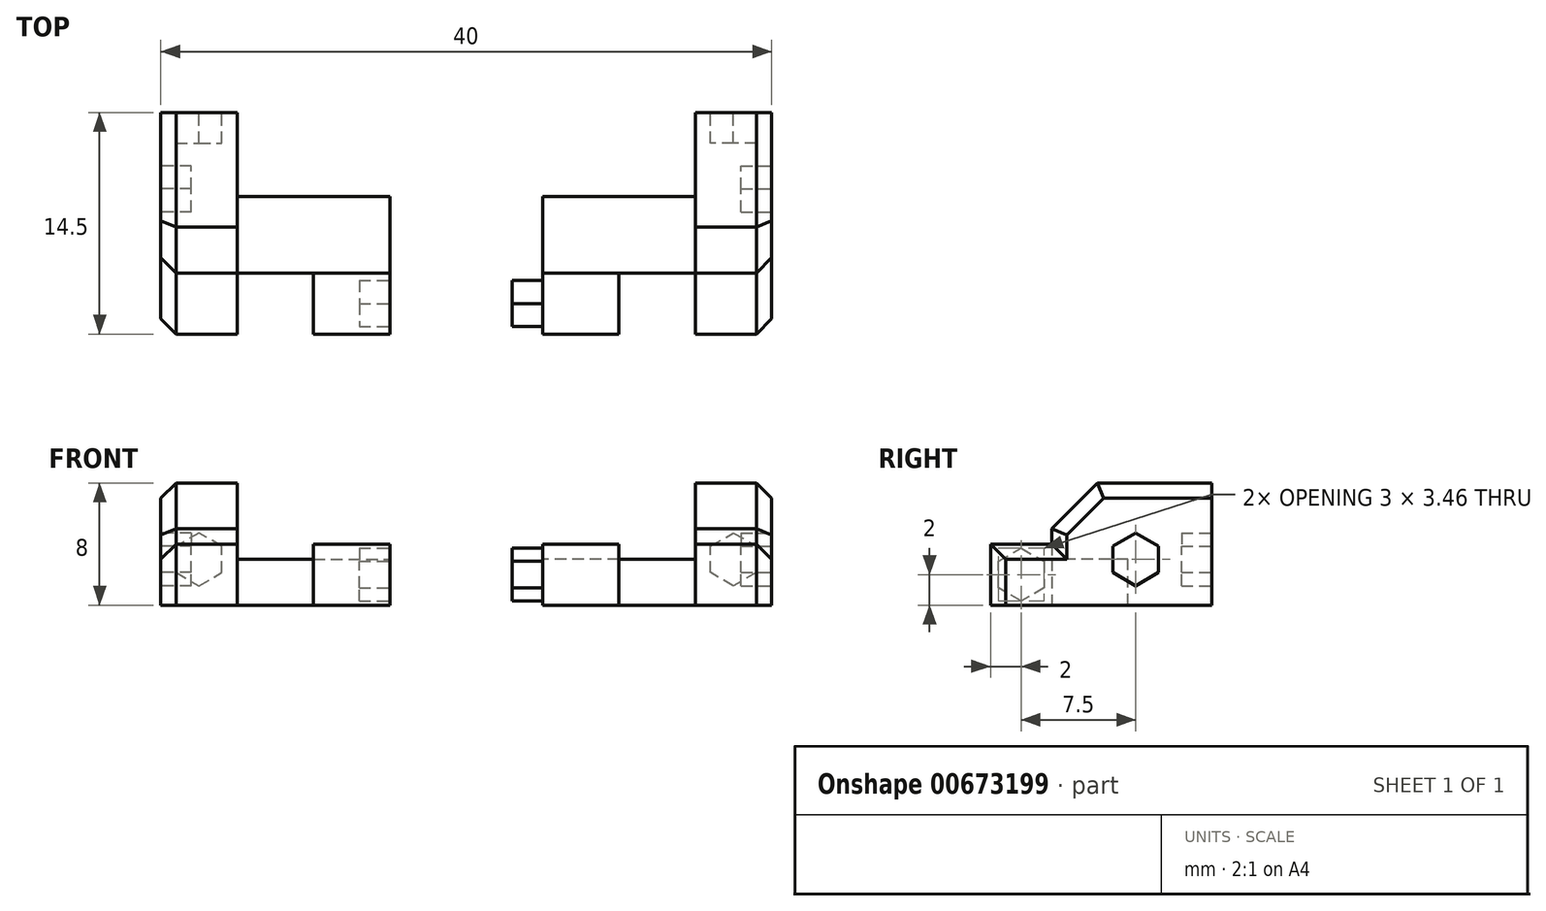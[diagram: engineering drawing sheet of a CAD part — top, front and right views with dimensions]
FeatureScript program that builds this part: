
annotation { "Feature Type Name" : "Feature", "Feature Type Description" : "" }
export const myFeature = defineFeature(function(context is Context, id is Id, definition is map)
    precondition{}
    {
        {
            var Q0;
            Q0=qCreatedBy(makeId("Right.planeOp"),FACE);
            var sketch = newSketch(context, id + "F0", { "sketchPlane" : qUnion([Q0])});
            skLineSegment(sketch, "E0.1", {"start": v(1, 13) * mm, "end": v(1, 1) * mm, "construction": true});
            skLineSegment(sketch, "E1.MirrorCS", {"start": v(-24.5, 7) * mm, "end": v(-24.5, 10) * mm});
            skLineSegment(sketch, "E2.MirrorCS", {"start": v(-28.5, 0) * mm, "end": v(-29.5, 1) * mm, "construction": true});
            skLineSegment(sketch, "E3.MirrorCS", {"start": v(-29.5, 10) * mm, "end": v(-29.5, 12) * mm});
            skLineSegment(sketch, "E4.MirrorCS", {"start": v(1, 1) * mm, "end": v(0, 0) * mm, "construction": true});
            skLineSegment(sketch, "E5.MirrorCS", {"start": v(-29.5, 12) * mm, "end": v(-26.5, 15) * mm});
            skLineSegment(sketch, "E6.MirrorCS", {"start": v(-1, 15) * mm, "end": v(1, 13) * mm, "construction": true});
            skLineSegment(sketch, "E7.MirrorCS", {"start": v(-29.5, 7) * mm, "end": v(-24.5, 7) * mm});
            skLineSegment(sketch, "E8.MirrorCS", {"start": v(-29.5, 1) * mm, "end": v(-29.5, 7) * mm, "construction": true});
            skLineSegment(sketch, "E9.MirrorCS", {"start": v(0, 0) * mm, "end": v(-28.5, 0) * mm, "construction": true});
            skLineSegment(sketch, "E10.MirrorCS", {"start": v(-26.5, 15) * mm, "end": v(-1, 15) * mm, "construction": true});
            skLineSegment(sketch, "E11.MirrorCS", {"start": v(-24.5, 10) * mm, "end": v(-29.5, 10) * mm});
            skLineSegment(sketch, "E12", {"start": v(-29.5, 10) * mm, "end": v(-33.5, 10) * mm});
            skLineSegment(sketch, "E13", {"start": v(-33.5, 10) * mm, "end": v(-33.5, 7) * mm});
            skLineSegment(sketch, "E14", {"start": v(-33.5, 7) * mm, "end": v(-29.5, 7) * mm});
            skLineSegment(sketch, "E15", {"start": v(-27, 10) * mm, "end": v(-27, 13) * mm});
            skLineSegment(sketch, "E16", {"start": v(-27, 13) * mm, "end": v(-19, 13) * mm});
            skLineSegment(sketch, "E17", {"start": v(-19, 13) * mm, "end": v(-19, 7) * mm});
            skPoint(sketch, "E18.endSnap0", {"position": v(-27, 7) * mm});
            skLineSegment(sketch, "E19", {"start": v(-24.5, 7) * mm, "end": v(-19, 7) * mm});
            skPoint(sketch, "E20.start.orphan", {"position": v(-27, 4) * mm});
            skLineSegment(sketch, "E21", {"start": v(-29.5, 10) * mm, "end": v(-29.5, 7) * mm});
            skLineSegment(sketch, "E22", {"start": v(-26.5, 15) * mm, "end": v(-19, 15) * mm});
            skLineSegment(sketch, "E23", {"start": v(-19, 15) * mm, "end": v(-19, 13) * mm});
            skSolve(sketch);
        }
        {
            var Q0;
            Q0=qSketchRegion(id+"F0",true);
            extrude(context, id + "F1", {"entities" : qUnion([Q0]), "oppositeDirection" : true, "depth" : 5 * mm});
        }
        {
            var Q0;
            {var subQ3=sQuery(id+"F0.wireOp",EDGE,"E1.MirrorCS");Q0=makeQuery(id+"F0.imprint","IMPRINT",FACE,{"disambiguationData":[TD([[makeQuery(id+"F0.imprint","IMPRINT",EDGE,{"derivedFrom":subQ3}),1.0]])]});}
            extrude(context, id + "F2", {"entities" : qUnion([Q0]), "operationType" : NewBodyOperationType.ADD, "depth" : 10 * mm});
        }
        {
            var Q0;
            Q0=makeQuery(id+"F2.opExtrude","SWEPT_FACE",FACE,{"disambiguationData":[OSD([sQuery(id+"F0.wireOp",EDGE,"E21")])]});
            var sketch = newSketch(context, id + "F3", { "sketchPlane" : qUnion([Q0])});
            skLineSegment(sketch, "E24.bottom", {"start": v(10, 7) * mm, "end": v(5, 7) * mm});
            skLineSegment(sketch, "E24.top", {"start": v(10, 10) * mm, "end": v(5, 10) * mm});
            skLineSegment(sketch, "E24.left", {"start": v(10, 7) * mm, "end": v(10, 10) * mm});
            skLineSegment(sketch, "E24.right", {"start": v(5, 7) * mm, "end": v(5, 10) * mm});
            skSolve(sketch);
        }
        {
            var Q0;
            Q0=qSketchRegion(id+"F3",true);
            extrude(context, id + "F4", {"entities" : qUnion([Q0]), "operationType" : NewBodyOperationType.ADD, "depth" : 4 * mm});
        }
        {
            var Q0;
            {var subQ0=sQuery(id+"F0.wireOp",EDGE,"E11.MirrorCS");Q0=makeQuery(id+"F4.boolean.opBoolean","MERGE",FACE,{"derivedFrom":[makeQuery(id+"F2.boolean.opBoolean","MERGE",FACE,{"derivedFrom":[makeQuery(id+"F1.opExtrude","SWEPT_FACE",FACE,{"disambiguationData":[OSD([subQ0,sQuery(id+"F0.wireOp",EDGE,"E12")])]}),makeQuery(id+"F2.opExtrude","SWEPT_FACE",FACE,{"disambiguationData":[OSD([subQ0])]})]}),makeQuery(id+"F4.opExtrude","SWEPT_FACE",FACE,{"disambiguationData":[OSD([sQuery(id+"F3.wireOp",EDGE,"E24.top")])]})]});}
            var sketch = newSketch(context, id + "F5", { "sketchPlane" : qUnion([Q0])});
            skLineSegment(sketch, "E25", {"start": v(5, -29.5) * mm, "end": v(10, -29.5) * mm});
            skSolve(sketch);
        }
        {
            var Q0;
            {var subQ0=sQuery(id+"F5.wireOp",EDGE,"E25");Q0=makeQuery(id+"F5.imprint","IMPRINT",FACE,{"disambiguationData":[TD([[makeQuery(id+"F5.imprint","IMPRINT",EDGE,{"derivedFrom":subQ0}),-1.0]])]});}
            extrude(context, id + "F6", {"entities" : qUnion([Q0]), "operationType" : NewBodyOperationType.ADD, "depth" : 1 * mm});
        }
        {
            var Q0;
            {var subQ0=sQuery(id+"F3.wireOp",EDGE,"E24.left");var subQ1=sQuery(id+"F0.wireOp",EDGE,"E11.MirrorCS");Q0=makeQuery(id+"F6.boolean.opBoolean","MERGE",FACE,{"derivedFrom":[makeQuery(id+"F4.boolean.opBoolean","MERGE",FACE,{"derivedFrom":[makeQuery(id+"F2.opExtrude","CAP_FACE",FACE,{"disambiguationData":[OSD([sQuery(id+"F0.wireOp",EDGE,"E1.MirrorCS"),sQuery(id+"F0.wireOp",EDGE,"E7.MirrorCS"),subQ1,sQuery(id+"F0.wireOp",EDGE,"E21")])],"isStart":false}),makeQuery(id+"F4.opExtrude","SWEPT_FACE",FACE,{"disambiguationData":[OSD([subQ0])]})]}),makeQuery(id+"F6.opExtrude","SWEPT_FACE",FACE,{"disambiguationData":[OSD([subQ1,sQuery(id+"F3.wireOp",EDGE,"E24.top"),subQ0])]})]});}
            var sketch = newSketch(context, id + "F7", { "sketchPlane" : qUnion([Q0])});
            skLineSegment(sketch, "E26.bottom", {"start": v(-33.5, 11) * mm, "end": v(-29.5, 11) * mm, "construction": true});
            skLineSegment(sketch, "E26.top", {"start": v(-33.5, 7) * mm, "end": v(-29.5, 7) * mm, "construction": true});
            skLineSegment(sketch, "E26.left", {"start": v(-33.5, 11) * mm, "end": v(-33.5, 7) * mm, "construction": true});
            skLineSegment(sketch, "E26.right", {"start": v(-29.5, 11) * mm, "end": v(-29.5, 7) * mm, "construction": true});
            skCircle(sketch, "E27.cCircle", {"center": v(-31.5, 9) * mm, "radius": 1.5 * mm, "construction": true});
            skPoint(sketch, "E27.cCircle.centerSnap0", {"position": v(-31.5, 11) * mm});
            skPoint(sketch, "E27.cCircle.centerSnap1", {"position": v(-29.5, 9) * mm});
            skLineSegment(sketch, "E27.0", {"start": v(-33, 8.13) * mm, "end": v(-33, 9.87) * mm});
            skLineSegment(sketch, "E27.1", {"start": v(-33, 9.87) * mm, "end": v(-31.5, 10.73) * mm});
            skLineSegment(sketch, "E27.2", {"start": v(-31.5, 10.73) * mm, "end": v(-30, 9.87) * mm});
            skLineSegment(sketch, "E27.3", {"start": v(-30, 9.87) * mm, "end": v(-30, 8.13) * mm});
            skLineSegment(sketch, "E27.4", {"start": v(-30, 8.13) * mm, "end": v(-31.5, 7.27) * mm});
            skLineSegment(sketch, "E27.5", {"start": v(-31.5, 7.27) * mm, "end": v(-33, 8.13) * mm});
            skPoint(sketch, "E27.0.midPoint", {"position": v(-33, 9) * mm});
            skSolve(sketch);
        }
        {
            var Q0;
            Q0=qSketchRegion(id+"F7",true);
            extrude(context, id + "F8", {"entities" : qUnion([Q0]), "operationType" : NewBodyOperationType.REMOVE, "oppositeDirection" : true, "depth" : 2 * mm});
        }
        {
            var Q0;
            Q0=makeQuery(id+"F1.opExtrude","SWEPT_FACE",FACE,{"disambiguationData":[OSD([sQuery(id+"F0.wireOp",EDGE,"E17")])]});
            var sketch = newSketch(context, id + "F9", { "sketchPlane" : qUnion([Q0])});
            skLineSegment(sketch, "E28.bottom", {"start": v(0, 7) * mm, "end": v(5, 7) * mm, "construction": true});
            skLineSegment(sketch, "E28.top", {"start": v(0, 7) * mm, "end": v(5, 7) * mm, "construction": true});
            skLineSegment(sketch, "E28.left", {"start": v(0, 7) * mm, "end": v(0, 7) * mm});
            skLineSegment(sketch, "E28.right", {"start": v(5, 7) * mm, "end": v(5, 7) * mm});
            skPoint(sketch, "E29.cCircle.centerSnap0", {"position": v(2.5, 7) * mm});
            skPoint(sketch, "E29.cCircle.centerSnap1", {"position": v(5, 11) * mm});
            skLineSegment(sketch, "E29.0", {"start": v(1, 9.13) * mm, "end": v(1, 10.87) * mm});
            skLineSegment(sketch, "E29.1", {"start": v(1, 10.87) * mm, "end": v(2.5, 11.73) * mm});
            skLineSegment(sketch, "E29.2", {"start": v(2.5, 11.73) * mm, "end": v(4, 10.87) * mm});
            skLineSegment(sketch, "E29.3", {"start": v(4, 10.87) * mm, "end": v(4, 9.13) * mm});
            skLineSegment(sketch, "E29.4", {"start": v(4, 9.13) * mm, "end": v(2.5, 8.27) * mm});
            skLineSegment(sketch, "E29.5", {"start": v(2.5, 8.27) * mm, "end": v(1, 9.13) * mm});
            skPoint(sketch, "E29.0.midPoint", {"position": v(1, 10) * mm});
            skSolve(sketch);
        }
        {
            var Q0;
            Q0=qSketchRegion(id+"F9",true);
            extrude(context, id + "F10", {"entities" : qUnion([Q0]), "operationType" : NewBodyOperationType.REMOVE, "oppositeDirection" : true, "depth" : 2 * mm});
        }
        {
            var Q0;
            Q0=makeQuery(id+"F1.opExtrude","CAP_FACE",FACE,{"disambiguationData":[OSD([sQuery(id+"F0.wireOp",EDGE,"E7.MirrorCS"),sQuery(id+"F0.wireOp",EDGE,"E11.MirrorCS"),sQuery(id+"F0.wireOp",EDGE,"E12"),sQuery(id+"F0.wireOp",EDGE,"E13"),sQuery(id+"F0.wireOp",EDGE,"E14"),sQuery(id+"F0.wireOp",EDGE,"E15"),sQuery(id+"F0.wireOp",EDGE,"E16"),sQuery(id+"F0.wireOp",EDGE,"E17"),sQuery(id+"F0.wireOp",EDGE,"E19")])],"isStart":false});
            var sketch = newSketch(context, id + "F11", { "sketchPlane" : qUnion([Q0])});
            skLineSegment(sketch, "E30.bottom", {"start": v(27, 13) * mm, "end": v(21, 13) * mm, "construction": true});
            skLineSegment(sketch, "E30.top", {"start": v(27, 7) * mm, "end": v(21, 7) * mm, "construction": true});
            skLineSegment(sketch, "E30.left", {"start": v(27, 13) * mm, "end": v(27, 7) * mm, "construction": true});
            skLineSegment(sketch, "E30.right", {"start": v(21, 13) * mm, "end": v(21, 7) * mm, "construction": true});
            skPoint(sketch, "E31.cCircle.centerSnap0", {"position": v(24, 13) * mm});
            skLineSegment(sketch, "E31.0", {"start": v(22.5, 9.13) * mm, "end": v(22.5, 10.87) * mm});
            skLineSegment(sketch, "E31.1", {"start": v(22.5, 10.87) * mm, "end": v(24, 11.73) * mm});
            skLineSegment(sketch, "E31.2", {"start": v(24, 11.73) * mm, "end": v(25.5, 10.87) * mm});
            skLineSegment(sketch, "E31.3", {"start": v(25.5, 10.87) * mm, "end": v(25.5, 9.13) * mm});
            skLineSegment(sketch, "E31.4", {"start": v(25.5, 9.13) * mm, "end": v(24, 8.27) * mm});
            skLineSegment(sketch, "E31.5", {"start": v(24, 8.27) * mm, "end": v(22.5, 9.13) * mm});
            skPoint(sketch, "E31.0.midPoint", {"position": v(22.5, 10) * mm});
            skSolve(sketch);
        }
        {
            var Q0;
            Q0=qSketchRegion(id+"F11",true);
            extrude(context, id + "F12", {"entities" : qUnion([Q0]), "operationType" : NewBodyOperationType.REMOVE, "oppositeDirection" : true, "depth" : 2 * mm});
        }
        {
            var Q0;
            {var subQ0=sQuery(id+"F0.wireOp",EDGE,"E11.MirrorCS");Q0=makeQuery(id+"F4.boolean.opBoolean","MERGE",FACE,{"derivedFrom":[makeQuery(id+"F2.boolean.opBoolean","MERGE",FACE,{"derivedFrom":[makeQuery(id+"F1.opExtrude","SWEPT_FACE",FACE,{"disambiguationData":[OSD([subQ0,sQuery(id+"F0.wireOp",EDGE,"E12")])]}),makeQuery(id+"F2.opExtrude","SWEPT_FACE",FACE,{"disambiguationData":[OSD([subQ0])]})]}),makeQuery(id+"F4.opExtrude","SWEPT_FACE",FACE,{"disambiguationData":[OSD([sQuery(id+"F3.wireOp",EDGE,"E24.top")])]})]});}
            var sketch = newSketch(context, id + "F13", { "sketchPlane" : qUnion([Q0])});
            skLineSegment(sketch, "E32.bottom", {"start": v(0, -33.5) * mm, "end": v(-5, -33.5) * mm});
            skLineSegment(sketch, "E32.top", {"start": v(0, -29.5) * mm, "end": v(-5, -29.5) * mm});
            skLineSegment(sketch, "E32.left", {"start": v(0, -33.5) * mm, "end": v(0, -29.5) * mm});
            skLineSegment(sketch, "E32.right", {"start": v(-5, -33.5) * mm, "end": v(-5, -29.5) * mm});
            skSolve(sketch);
        }
        {
            var Q0;
            Q0=qSketchRegion(id+"F13",true);
            extrude(context, id + "F14", {"entities" : qUnion([Q0]), "operationType" : NewBodyOperationType.ADD, "depth" : 1 * mm});
        }
        {
            var Q0;
            Q0=qCreatedBy(makeId("Right.planeOp"),FACE);
            cPlane(context, id + "F15", {"entities" : qUnion([Q0]), "cplaneType" : CPlaneType.OFFSET, "offset" : 15 * mm, "width" : 150 * mm, "height" : 150 * mm});
        }
        {
            var Q0;
            Q0=makeQuery(id+"F1.opExtrude","SWEPT_BODY",BODY,{"disambiguationData":[OSD([sQuery(id+"F0.wireOp",EDGE,"E7.MirrorCS"),sQuery(id+"F0.wireOp",EDGE,"E11.MirrorCS"),sQuery(id+"F0.wireOp",EDGE,"E12"),sQuery(id+"F0.wireOp",EDGE,"E13"),sQuery(id+"F0.wireOp",EDGE,"E14"),sQuery(id+"F0.wireOp",EDGE,"E15"),sQuery(id+"F0.wireOp",EDGE,"E16"),sQuery(id+"F0.wireOp",EDGE,"E17"),sQuery(id+"F0.wireOp",EDGE,"E19")])]});
            var Q1;
            Q1=qCreatedBy(id+"F15.planeOp",FACE);
            mirror(context, id + "F16", {"entities" : qUnion([Q0]), "mirrorPlane" : qUnion([Q1])});
        }
        {
            var Q0;
            Q0=makeQuery(id+"F16.opPattern","COPY",FACE,{"derivedFrom":makeQuery(id+"F8.boolean.opBoolean","COPY",FACE,{"derivedFrom":makeQuery(id+"F8.opExtrude","CAP_FACE",FACE,{"disambiguationData":[OSD([sQuery(id+"F7.wireOp",EDGE,"E27.0"),sQuery(id+"F7.wireOp",EDGE,"E27.1"),sQuery(id+"F7.wireOp",EDGE,"E27.2"),sQuery(id+"F7.wireOp",EDGE,"E27.3"),sQuery(id+"F7.wireOp",EDGE,"E27.4"),sQuery(id+"F7.wireOp",EDGE,"E27.5")])],"isStart":false})}),"instanceName":"1"});
            extrude(context, id + "F17", {"entities" : qUnion([Q0]), "operationType" : NewBodyOperationType.ADD, "depth" : 4 * mm});
        }
        {
            var Q0;
            Q0=makeQuery(id+"F1.opExtrude","CAP_EDGE",EDGE,{"disambiguationData":[OSD([sQuery(id+"F0.wireOp",EDGE,"E22")])],"isStart":false});
            var Q1;
            Q1=makeQuery(id+"F1.opExtrude","CAP_EDGE",EDGE,{"disambiguationData":[OSD([sQuery(id+"F0.wireOp",EDGE,"E5.MirrorCS")])],"isStart":false});
            var Q2;
            Q2=makeQuery(id+"F14.opExtrude","CAP_EDGE",EDGE,{"disambiguationData":[OSD([sQuery(id+"F13.wireOp",EDGE,"E32.right")])],"isStart":false});
            var Q3;
            Q3=makeQuery(id+"F14.boolean.opBoolean","MERGE",EDGE,{"derivedFrom":[makeQuery(id+"F1.opExtrude","CAP_EDGE",EDGE,{"disambiguationData":[OSD([sQuery(id+"F0.wireOp",EDGE,"E13")])],"isStart":false}),makeQuery(id+"F14.opExtrude","SWEPT_EDGE",EDGE,{"disambiguationData":[OSD([sQuery(id+"F13.wireOp",EDGE,"E32.bottom"),sQuery(id+"F13.wireOp",EDGE,"E32.right")])]})]});
            var Q4;
            Q4=makeQuery(id+"F1.opExtrude","CAP_EDGE",EDGE,{"disambiguationData":[OSD([sQuery(id+"F0.wireOp",EDGE,"E3.MirrorCS")])],"isStart":false});
            var Q5;
            Q5=makeQuery(id+"F16.opPattern","COPY",EDGE,{"derivedFrom":makeQuery(id+"F14.boolean.opBoolean","MERGE",EDGE,{"derivedFrom":[makeQuery(id+"F1.opExtrude","CAP_EDGE",EDGE,{"disambiguationData":[OSD([sQuery(id+"F0.wireOp",EDGE,"E13")])],"isStart":false}),makeQuery(id+"F14.opExtrude","SWEPT_EDGE",EDGE,{"disambiguationData":[OSD([sQuery(id+"F13.wireOp",EDGE,"E32.bottom"),sQuery(id+"F13.wireOp",EDGE,"E32.right")])]})]}),"instanceName":"1"});
            var Q6;
            Q6=makeQuery(id+"F16.opPattern","COPY",EDGE,{"derivedFrom":makeQuery(id+"F14.opExtrude","CAP_EDGE",EDGE,{"disambiguationData":[OSD([sQuery(id+"F13.wireOp",EDGE,"E32.right")])],"isStart":false}),"instanceName":"1"});
            var Q7;
            Q7=makeQuery(id+"F16.opPattern","COPY",EDGE,{"derivedFrom":makeQuery(id+"F1.opExtrude","CAP_EDGE",EDGE,{"disambiguationData":[OSD([sQuery(id+"F0.wireOp",EDGE,"E3.MirrorCS")])],"isStart":false}),"instanceName":"1"});
            var Q8;
            Q8=makeQuery(id+"F16.opPattern","COPY",EDGE,{"derivedFrom":makeQuery(id+"F1.opExtrude","CAP_EDGE",EDGE,{"disambiguationData":[OSD([sQuery(id+"F0.wireOp",EDGE,"E5.MirrorCS")])],"isStart":false}),"instanceName":"1"});
            var Q9;
            Q9=makeQuery(id+"F16.opPattern","COPY",EDGE,{"derivedFrom":makeQuery(id+"F1.opExtrude","CAP_EDGE",EDGE,{"disambiguationData":[OSD([sQuery(id+"F0.wireOp",EDGE,"E22")])],"isStart":false}),"instanceName":"1"});
            chamfer(context, id + "F18", {"entities" : qUnion([Q0, Q1, Q2, Q3, Q4, Q5, Q6, Q7, Q8, Q9]), "width" : 1 * mm, "tangentPropagation" : true});
        }
    });
